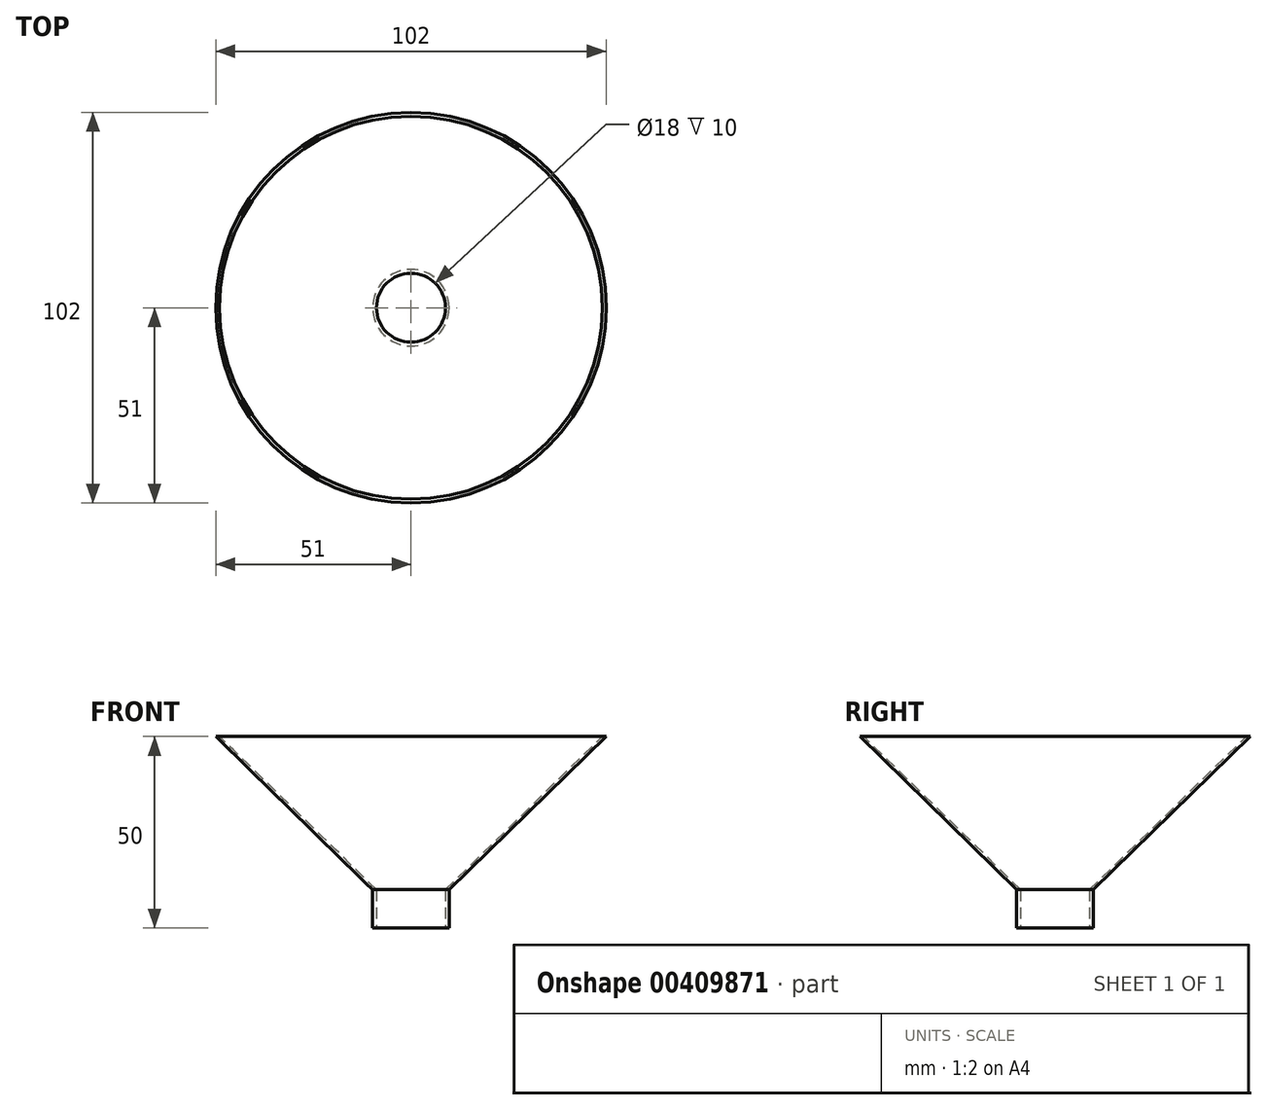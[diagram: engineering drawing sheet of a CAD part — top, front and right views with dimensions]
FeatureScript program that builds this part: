
annotation { "Feature Type Name" : "Feature", "Feature Type Description" : "" }
export const myFeature = defineFeature(function(context is Context, id is Id, definition is map)
    precondition{}
    {
        {
            var Q0;
            Q0=qCreatedBy(makeId("Top.planeOp"),FACE);
            var sketch = newSketch(context, id + "F0", { "sketchPlane" : qUnion([Q0])});
            skCircle(sketch, "E0", {"center": v(0, 0) * mm, "radius": 9 * mm});
            skCircle(sketch, "E1.0", {"center": v(0, 0) * mm, "radius": 10 * mm});
            skSolve(sketch);
        }
        {
            var Q0;
            Q0 = qSketchRegion(id + "F0", true);
            extrude(context, id + "F1", {"entities" : qUnion([Q0]), "depth" : 10 * mm});
        }
        {
            var Q0;
            Q0=qCreatedBy(makeId("Top.planeOp"),FACE);
            cPlane(context, id + "F2", {"entities" : qUnion([Q0]), "cplaneType" : CPlaneType.OFFSET, "offset" : 50 * mm, "width" : 150 * mm, "height" : 150 * mm});
        }
        {
            var Q0;
            Q0=qCreatedBy(id+"F2.planeOp",FACE);
            var sketch = newSketch(context, id + "F3", { "sketchPlane" : qUnion([Q0])});
            skCircle(sketch, "E2", {"center": v(0, 0) * mm, "radius": 50 * mm});
            skSolve(sketch);
        }
        {
            var Q0;
            Q0=makeQuery(id+"F1.opExtrude","CAP_FACE",FACE,{"disambiguationData":[OSD([sQuery(id+"F0.wireOp",EDGE,"E0"),sQuery(id+"F0.wireOp",EDGE,"E1.0")])],"isStart":false});
            var sketch = newSketch(context, id + "F4", { "sketchPlane" : qUnion([Q0])});
            skCircle(sketch, "E3.0", {"center": v(0, 0) * mm, "radius": 9 * mm});
            skSolve(sketch);
        }
        {
            var Q0;
            Q0=makeQuery(id+"F3.imprint","IMPRINT",FACE,{"disambiguationData":[TD([[makeQuery(id+"F3.imprint","IMPRINT",EDGE,{"derivedFrom":sQuery(id+"F3.wireOp",EDGE,"E2")}),1.0]])]});
            var sketch = newSketch(context, id + "F5", { "sketchPlane" : qUnion([Q0])});
            skCircle(sketch, "E4.0", {"center": v(0, 0) * mm, "radius": 51 * mm});
            skSolve(sketch);
        }
        {
            var Q0;
            Q0=makeQuery(id+"F4.imprint","IMPRINT",FACE,{"disambiguationData":[TD([[makeQuery(id+"F4.imprint","IMPRINT",EDGE,{"derivedFrom":sQuery(id+"F4.wireOp",EDGE,"E3.0")}),1.0]])]});
            var sketch = newSketch(context, id + "F6", { "sketchPlane" : qUnion([Q0])});
            skCircle(sketch, "E5.0", {"center": v(0, 0) * mm, "radius": 10 * mm});
            skSolve(sketch);
        }
        {
            var Q0;
            Q0=qCreatedBy(makeId("Right.planeOp"),FACE);
            var sketch = newSketch(context, id + "F7", { "sketchPlane" : qUnion([Q0])});
            skLineSegment(sketch, "E6", {"start": v(51, 50) * mm, "end": v(10, 10) * mm});
            skLineSegment(sketch, "E7", {"start": v(50, 50) * mm, "end": v(9, 10) * mm});
            skLineSegment(sketch, "E8", {"start": v(10, 10) * mm, "end": v(9, 10) * mm});
            skLineSegment(sketch, "E9", {"start": v(51, 50) * mm, "end": v(50, 50) * mm});
            skSolve(sketch);
        }
        {
            var Q0;
            Q0=makeQuery(id+"F7.imprint","IMPRINT",FACE,{"disambiguationData":[TD([[makeQuery(id+"F7.imprint","IMPRINT",EDGE,{"derivedFrom":sQuery(id+"F7.wireOp",EDGE,"E6")}),-1.0]])]});
            var Q1;
            Q1=sQuery(id+"F3.wireOp",EDGE,"E2");
            revolve(context, id + "F8", {"entities" : qUnion([Q0]), "axis" : qUnion([Q1]), "revolveType" : RevolveType.FULL});
        }
    });
